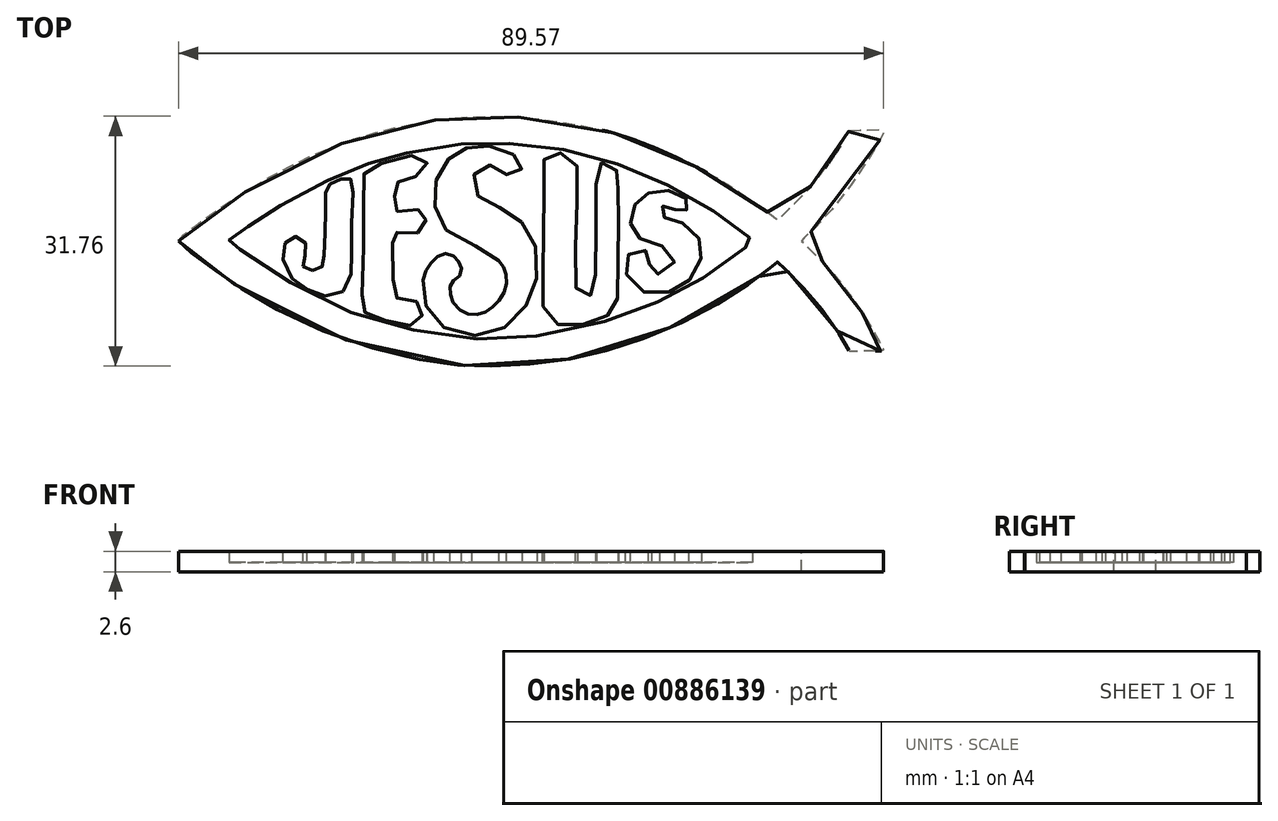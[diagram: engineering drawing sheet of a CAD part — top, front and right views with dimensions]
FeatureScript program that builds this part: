
annotation { "Feature Type Name" : "Feature", "Feature Type Description" : "" }
export const myFeature = defineFeature(function(context is Context, id is Id, definition is map)
    precondition{}
    {
        {
            var Q0;
            Q0=qCreatedBy(makeId("Top.planeOp"),FACE);
            var sketch = newSketch(context, id + "F0", { "sketchPlane" : qUnion([Q0])});
            skFitSpline(sketch, "E0", {"points": [v(-43.03, -3.62) * mm, v(-42.38, -2.84) * mm, v(-37.2, 0.93) * mm, v(-30.34, 5.1) * mm, v(-21.88, 8.93) * mm, v(-14.04, 11.08) * mm, v(-9.02, 11.9) * mm, v(-3.63, 12.23) * mm, v(1.53, 12) * mm, v(8.98, 10.89) * mm, v(15.28, 9.1) * mm, v(20.7, 6.77) * mm, v(25.92, 4.06) * mm, v(29.84, 1.42) * mm, v(33.04, -0.93) * mm, v(33.1, -0.98) * mm, v(33.75, -0.29) * mm, v(36.88, 2.85) * mm, v(40.06, 7.06) * mm, v(41.93, 9.97) * mm, v(42.02, 10.2) * mm, v(42.17, 10.43) * mm, v(42.33, 10.47) * mm, v(46.48, 10.48) * mm, v(46.54, 10.43) * mm, v(46.52, 10.18) * mm, v(46.38, 9.82) * mm, v(41.74, 2.58) * mm, v(36.58, -3.1) * mm, v(36.2, -3.43) * mm, v(36.12, -3.55) * mm, v(36.11, -3.7) * mm, v(36.24, -3.81) * mm, v(38.25, -5.72) * mm, v(39.49, -7.04) * mm, v(41.53, -9.51) * mm, v(43.94, -12.91) * mm, v(45.57, -15.69) * mm, v(46.5, -17.42) * mm, v(46.5, -17.5) * mm, v(46.5, -17.57) * mm, v(46.44, -17.61) * mm, v(46.34, -17.62) * mm, v(42.46, -17.66) * mm, v(42.32, -17.67) * mm, v(42.21, -17.62) * mm, v(42.1, -17.47) * mm, v(40.97, -15.51) * mm, v(38.03, -11.5) * mm, v(35.22, -8.38) * mm, v(33.32, -6.51) * mm, v(33.2, -6.4) * mm, v(33.08, -6.3) * mm, v(32.98, -6.32) * mm, v(32.85, -6.44) * mm, v(32.35, -6.87) * mm, v(29.21, -9.19) * mm, v(22.42, -13.24) * mm, v(13.63, -16.82) * mm, v(5.87, -18.74) * mm, v(-3.14, -19.52) * mm, v(-9.65, -19.13) * mm, v(-22.06, -16.05) * mm, v(-33.94, -10.36) * mm, v(-38.84, -7) * mm, v(-42.36, -4.39) * mm, v(-43.03, -3.62) * mm]});
            skFitSpline(sketch, "E1", {"points": [v(-35.2, -4.7) * mm, v(-35.9, -4.22) * mm, v(-36.47, -3.8) * mm, v(-36.56, -3.67) * mm, v(-36.58, -3.52) * mm, v(-35.6, -2.74) * mm, v(-34.47, -2) * mm, v(-32.32, -0.52) * mm, v(-27.46, 2.4) * mm, v(-21.27, 5.33) * mm, v(-17.87, 6.52) * mm, v(-13.87, 7.58) * mm, v(-6.3, 8.78) * mm, v(-0.7, 8.74) * mm, v(6.77, 7.83) * mm, v(14.12, 5.62) * mm, v(20.76, 2.67) * mm, v(26.51, -0.93) * mm, v(29.62, -3.31) * mm, v(29.8, -3.47) * mm, v(29.85, -3.57) * mm, v(29.87, -3.72) * mm, v(29.66, -3.94) * mm, v(25.66, -6.96) * mm, v(19.56, -10.48) * mm, v(13.23, -13.2) * mm, v(2.03, -15.78) * mm, v(-6.73, -15.92) * mm, v(-17.35, -13.94) * mm, v(-26.92, -10) * mm, v(-35.2, -4.7) * mm]});
            skSolve(sketch);
        }
        {
            var Q0;
            Q0=makeQuery(id+"F0.imprint","IMPRINT",FACE,{"disambiguationData":[TD([[makeQuery(id+"F0.imprint","IMPRINT",EDGE,{"derivedFrom":sQuery(id+"F0.wireOp",EDGE,"E0")}),-1.0]])]});
            var Q1;
            Q1=makeQuery(id+"F0.imprint","IMPRINT",FACE,{"disambiguationData":[TD([[makeQuery(id+"F0.imprint","IMPRINT",EDGE,{"derivedFrom":sQuery(id+"F0.wireOp",EDGE,"E1")}),-1.0]])]});
            extrude(context, id + "F1", {"entities" : qUnion([Q0, Q1]), "oppositeDirection" : true, "depth" : 1.2 * mm, "offsetDistance" : 25 * mm});
        }
        {
            var Q0;
            Q0=makeQuery(id+"F0.imprint","IMPRINT",FACE,{"disambiguationData":[TD([[makeQuery(id+"F0.imprint","IMPRINT",EDGE,{"derivedFrom":sQuery(id+"F0.wireOp",EDGE,"E0")}),-1.0]])]});
            extrude(context, id + "F2", {"entities" : qUnion([Q0]), "operationType" : NewBodyOperationType.ADD, "depth" : 1.4 * mm, "offsetDistance" : 25 * mm});
        }
        {
            var Q0;
            Q0=makeQuery(id+"F0.imprint","IMPRINT",FACE,{"disambiguationData":[TD([[makeQuery(id+"F0.imprint","IMPRINT",EDGE,{"derivedFrom":sQuery(id+"F0.wireOp",EDGE,"E1")}),-1.0]])]});
            var sketch = newSketch(context, id + "F3", { "sketchPlane" : qUnion([Q0])});
            skFitSpline(sketch, "E2", {"points": [v(-26, -7.38) * mm, v(-26.55, -7.33) * mm, v(-26.93, -7.18) * mm, v(-27.18, -6.91) * mm, v(-27.28, -6.59) * mm, v(-27.2, -6.06) * mm, v(-26.96, -5.38) * mm, v(-26.77, -4.83) * mm, v(-26.77, -4.22) * mm, v(-27.04, -3.64) * mm, v(-27.52, -3.24) * mm, v(-28.09, -3.03) * mm, v(-28.64, -3.09) * mm, v(-29.23, -3.48) * mm, v(-29.65, -4.3) * mm, v(-29.82, -5.28) * mm, v(-29.56, -6.82) * mm, v(-28.67, -8.28) * mm, v(-27.76, -9.09) * mm, v(-26.28, -9.99) * mm, v(-25.14, -10.48) * mm, v(-23.7, -10.58) * mm, v(-22.46, -10.25) * mm, v(-21.52, -9.33) * mm, v(-21.12, -7.75) * mm, v(-21.06, -6.61) * mm, v(-21.03, -3.8) * mm, v(-21.01, 0) * mm, v(-20.86, 3.06) * mm, v(-20.9, 3.74) * mm, v(-21.12, 4.18) * mm, v(-21.4, 4.4) * mm, v(-21.74, 4.46) * mm, v(-22.16, 4.33) * mm, v(-22.7, 4.12) * mm, v(-23.37, 3.83) * mm, v(-23.8, 3.61) * mm, v(-24.14, 3.36) * mm, v(-24.3, 3.01) * mm, v(-24.37, 2.6) * mm, v(-24.4, 2.12) * mm, v(-24.36, 0.46) * mm, v(-24.39, -1.39) * mm, v(-24.4, -3.31) * mm, v(-24.52, -5.4) * mm, v(-24.57, -6.1) * mm, v(-24.65, -6.57) * mm, v(-24.79, -6.9) * mm, v(-25, -7.13) * mm, v(-25.44, -7.32) * mm, v(-26, -7.38) * mm]});
            skFitSpline(sketch, "E3", {"points": [v(-15.6, 2) * mm, v(-15.59, 2.62) * mm, v(-15.54, 3.28) * mm, v(-15.32, 3.68) * mm, v(-14.99, 3.98) * mm, v(-14.44, 4.2) * mm, v(-13.77, 4.4) * mm, v(-12.59, 4.61) * mm, v(-11.75, 5.03) * mm, v(-11.53, 5.6) * mm, v(-11.47, 6.67) * mm, v(-11.9, 7.3) * mm, v(-12.86, 7.34) * mm, v(-14.83, 6.87) * mm, v(-16.97, 6.3) * mm, v(-18.64, 5.76) * mm, v(-19.15, 5.45) * mm, v(-19.49, 4.9) * mm, v(-19.53, 3.94) * mm, v(-19.53, 0.53) * mm, v(-19.53, -2.75) * mm, v(-19.64, -8.13) * mm, v(-19.72, -11.46) * mm, v(-19.72, -12) * mm, v(-19.6, -12.36) * mm, v(-19.28, -12.76) * mm, v(-18.7, -13.12) * mm, v(-17.45, -13.53) * mm, v(-16.01, -13.9) * mm, v(-14.4, -14.25) * mm, v(-13.52, -14.38) * mm, v(-12.86, -14.29) * mm, v(-12.43, -13.83) * mm, v(-12.1, -13.12) * mm, v(-12, -12.62) * mm, v(-12.12, -11.93) * mm, v(-12.48, -11.5) * mm, v(-13.26, -11.2) * mm, v(-14.33, -11.09) * mm, v(-15.03, -10.96) * mm, v(-15.52, -10.76) * mm, v(-15.71, -10.42) * mm, v(-15.78, -9.9) * mm, v(-15.78, -7.28) * mm, v(-15.83, -4.31) * mm, v(-15.87, -3.13) * mm, v(-15.86, -2.86) * mm, v(-15.78, -2.65) * mm, v(-15.6, -2.55) * mm, v(-15.04, -2.56) * mm, v(-14.16, -2.61) * mm, v(-12.93, -2.63) * mm, v(-12.52, -2.59) * mm, v(-12.2, -2.46) * mm, v(-12, -2.15) * mm, v(-11.65, -1.1) * mm, v(-11.55, -0.41) * mm, v(-11.64, 0) * mm, v(-11.99, 0.31) * mm, v(-12.95, 0.3) * mm, v(-13.88, 0) * mm, v(-14.94, 0) * mm, v(-15.53, 0.4) * mm, v(-15.63, 0.93) * mm, v(-15.62, 1.42) * mm, v(-15.6, 2) * mm]});
            skFitSpline(sketch, "E4", {"points": [v(-2.38, -6.13) * mm, v(-2.9, -5.77) * mm, v(-4.54, -4.7) * mm, v(-6.8, -3.55) * mm, v(-8.9, -2.36) * mm, v(-9.95, -1.1) * mm, v(-10.4, 0.3) * mm, v(-10.6, 1.93) * mm, v(-10.52, 3.26) * mm, v(-10.05, 4.75) * mm, v(-9.44, 5.91) * mm, v(-8.65, 6.88) * mm, v(-8.06, 7.41) * mm, v(-7.1, 7.97) * mm, v(-6.09, 8.31) * mm, v(-5.15, 8.46) * mm, v(-3.84, 8.46) * mm, v(-2.64, 8.28) * mm, v(-1.06, 7.73) * mm, v(0, 6.97) * mm, v(0.54, 6.39) * mm, v(0.69, 5.78) * mm, v(0.5, 5.47) * mm, v(0, 5.04) * mm, v(-0.54, 4.69) * mm, v(-1.25, 4.75) * mm, v(-1.81, 5.13) * mm, v(-2.5, 5.63) * mm, v(-3.37, 6) * mm, v(-4.22, 5.95) * mm, v(-5.01, 5.55) * mm, v(-5.48, 4.88) * mm, v(-5.76, 3.7) * mm, v(-5.46, 2.62) * mm, v(-4.67, 1.83) * mm, v(-3.55, 1.23) * mm, v(-2.22, 0.6) * mm, v(-0.93, 0) * mm, v(0.3, -1) * mm, v(1.34, -2.14) * mm, v(2.12, -3.69) * mm, v(2.52, -5.94) * mm, v(2.5, -8.23) * mm, v(1.94, -10.01) * mm, v(1.25, -11.63) * mm, v(0, -13.27) * mm, v(-1.62, -14.62) * mm, v(-3.42, -15.48) * mm, v(-5.63, -15.64) * mm, v(-7.95, -15.2) * mm, v(-9.75, -14.3) * mm, v(-10.82, -13.2) * mm, v(-11.7, -11.56) * mm, v(-12.04, -10.2) * mm, v(-11.98, -8.57) * mm], "startDerivative": vector(-96.88, 67.95) * mm, "endDerivative": vector(10.35, 82.84) * mm});
            skPoint(sketch, "E5.6.internal.orphan", {"position": v(-7.47, -6.18) * mm});
            skPoint(sketch, "E5.7.internal.orphan", {"position": v(-7.19, -6.18) * mm});
            skPoint(sketch, "E6.end.orphan", {"position": v(-10.86, -6.18) * mm});
            skFitSpline(sketch, "E7", {"points": [v(-11.98, -8.57) * mm, v(-11.58, -7.38) * mm, v(-11.06, -6.58) * mm, v(-10.33, -5.78) * mm, v(-9.6, -5.28) * mm, v(-8.64, -5.23) * mm, v(-7.9, -5.68) * mm, v(-7.47, -6.18) * mm, v(-7.13, -6.77) * mm, v(-7.1, -7.58) * mm, v(-7.47, -8.17) * mm, v(-8.03, -8.57) * mm, v(-8.38, -9.03) * mm, v(-8.55, -9.59) * mm, v(-8.51, -10.37) * mm, v(-8.24, -11.28) * mm, v(-7.47, -12.21) * mm, v(-6.6, -12.81) * mm, v(-5.6, -12.96) * mm, v(-4.7, -12.86) * mm, v(-3.8, -12.48) * mm, v(-3.09, -11.97) * mm, v(-2.3, -11.17) * mm, v(-1.76, -10.26) * mm, v(-1.44, -9.35) * mm, v(-1.34, -8.22) * mm, v(-1.54, -7.4) * mm, v(-1.8, -6.79) * mm, v(-2.38, -6.13) * mm], "startDerivative": vector(5.03, 35.46) * mm, "endDerivative": vector(-20.76, 17.16) * mm});
            skFitSpline(sketch, "E8", {"points": [v(3.39, 2.36) * mm, v(3.38, 0.23) * mm, v(3.35, -2.21) * mm, v(3.3, -4.9) * mm, v(3.3, -7.21) * mm, v(3.13, -9.67) * mm, v(3.18, -11.26) * mm, v(3.38, -12.24) * mm, v(3.76, -13.1) * mm, v(4.32, -13.66) * mm, v(5.14, -14.19) * mm, v(6.02, -14.37) * mm, v(6.85, -14.42) * mm, v(7.92, -14.3) * mm, v(8.97, -14.07) * mm, v(10.21, -13.62) * mm, v(11.17, -13.25) * mm, v(11.83, -12.8) * mm, v(12.13, -12.54) * mm, v(12.46, -12.07) * mm, v(12.66, -11.61) * mm, v(12.75, -10.1) * mm, v(12.84, -7.62) * mm, v(12.82, -5.3) * mm, v(12.88, -3.3) * mm, v(12.86, -0.95) * mm, v(12.83, 1.04) * mm, v(12.81, 2.6) * mm, v(12.84, 3.91) * mm, v(12.85, 4.35) * mm, v(12.85, 4.8) * mm, v(12.75, 5.17) * mm, v(12.6, 5.36) * mm, v(12.36, 5.54) * mm, v(12, 5.78) * mm, v(11.62, 6) * mm, v(11.13, 6.23) * mm, v(10.67, 6.33) * mm, v(10.29, 6.26) * mm, v(10.1, 5.85) * mm, v(10.01, 5.03) * mm, v(10.04, 2.4) * mm, v(10.01, -0.55) * mm, v(10.02, -4.3) * mm, v(9.94, -7.37) * mm, v(9.96, -8.94) * mm, v(9.85, -9.85) * mm, v(9.66, -10.3) * mm, v(9.3, -10.51) * mm, v(8.82, -10.62) * mm, v(8.28, -10.54) * mm, v(7.9, -10.29) * mm, v(7.6, -9.87) * mm, v(7.38, -9.26) * mm, v(7.37, -6.57) * mm, v(7.4, -3.4) * mm, v(7.51, 0) * mm, v(7.59, 2.72) * mm, v(7.62, 5.16) * mm, v(7.55, 6.06) * mm, v(7.24, 7.04) * mm, v(6.56, 7.35) * mm, v(5.78, 7.54) * mm, v(5.01, 7.65) * mm, v(4.25, 7.75) * mm, v(3.71, 7.43) * mm, v(3.45, 7) * mm, v(3.35, 5.9) * mm, v(3.33, 5.43) * mm, v(3.39, 2.36) * mm]});
            skFitSpline(sketch, "E9", {"points": [v(18.4, -4.25) * mm, v(16.94, -3.87) * mm, v(15.62, -3.32) * mm, v(14.85, -2.68) * mm, v(14.44, -1.8) * mm, v(14.35, -0.8) * mm, v(14.59, 0.24) * mm, v(15.05, 1.12) * mm, v(15.66, 1.8) * mm, v(16.35, 2.3) * mm, v(17.16, 2.68) * mm, v(18.45, 2.9) * mm, v(19.51, 2.7) * mm, v(20.55, 2.3) * mm, v(21.38, 1.84) * mm, v(21.73, 1.36) * mm, v(21.74, 1) * mm, v(21.66, 0.6) * mm, v(21.45, 0.25) * mm, v(21.1, 0) * mm, v(20.79, 0) * mm, v(20.16, 0.3) * mm, v(19.7, 0.65) * mm, v(19.26, 0.84) * mm, v(18.8, 0.9) * mm, v(18.34, 0.74) * mm, v(18.1, 0.35) * mm, v(18.17, -0.3) * mm, v(18.81, -0.68) * mm, v(19.6, -0.9) * mm, v(20.6, -1.21) * mm, v(21.77, -1.78) * mm, v(22.85, -2.87) * mm, v(23.31, -4.02) * mm, v(23.4, -5.01) * mm, v(23.2, -6.32) * mm, v(22.62, -7.69) * mm, v(21.27, -9.1) * mm, v(20.14, -9.76) * mm, v(18.24, -10.31) * mm, v(16.6, -10.26) * mm, v(15.13, -9.57) * mm, v(14, -8.12) * mm, v(13.71, -6.8) * mm, v(13.9, -5.72) * mm, v(14.53, -4.95) * mm, v(15.45, -4.65) * mm, v(16.3, -4.83) * mm, v(16.9, -5.46) * mm, v(16.99, -6.3) * mm, v(16.74, -6.67) * mm, v(16.62, -7.14) * mm, v(17.05, -7.6) * mm, v(18.24, -7.82) * mm, v(19.4, -7.28) * mm, v(19.97, -6.16) * mm, v(19.5, -4.92) * mm, v(18.4, -4.25) * mm]});
            skSolve(sketch);
        }
        {
            var Q0;
            Q0=makeQuery(id+"F3.imprint","IMPRINT",FACE,{"disambiguationData":[TD([[makeQuery(id+"F3.imprint","IMPRINT",EDGE,{"derivedFrom":sQuery(id+"F3.wireOp",EDGE,"E2")}),1.0]])]});
            var Q1;
            Q1=makeQuery(id+"F3.imprint","IMPRINT",FACE,{"disambiguationData":[TD([[makeQuery(id+"F3.imprint","IMPRINT",EDGE,{"derivedFrom":sQuery(id+"F3.wireOp",EDGE,"E3")}),1.0]])]});
            var Q2;
            Q2=makeQuery(id+"F3.imprint","IMPRINT",FACE,{"disambiguationData":[TD([[makeQuery(id+"F3.imprint","IMPRINT",EDGE,{"derivedFrom":sQuery(id+"F3.wireOp",EDGE,"E4")}),-1.0]])]});
            var Q3;
            Q3=makeQuery(id+"F3.imprint","IMPRINT",FACE,{"disambiguationData":[TD([[makeQuery(id+"F3.imprint","IMPRINT",EDGE,{"derivedFrom":sQuery(id+"F3.wireOp",EDGE,"E8")}),1.0]])]});
            var Q4;
            Q4=makeQuery(id+"F3.imprint","IMPRINT",FACE,{"disambiguationData":[TD([[makeQuery(id+"F3.imprint","IMPRINT",EDGE,{"derivedFrom":sQuery(id+"F3.wireOp",EDGE,"E9")}),-1.0]])]});
            extrude(context, id + "F4", {"entities" : qUnion([Q0, Q1, Q2, Q3, Q4]), "operationType" : NewBodyOperationType.ADD, "depth" : 1.4 * mm, "offsetDistance" : 25 * mm});
        }
    });
